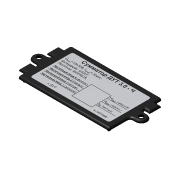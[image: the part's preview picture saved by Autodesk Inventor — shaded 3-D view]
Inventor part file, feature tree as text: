
AUTODESK INVENTOR PART (.ipt)
format: ipt  version: 2012 (Build 160160000, 160)  size: 340,480 bytes
history: native  units: mm
features: sketch x5, extrude x4, other x3, fillet x3
ambient origin geometry x8: Origin, YZ Plane, XZ Plane, XY Plane, X Axis, Y Axis, Z Axis, Center Point
feature tree (15):
  other  "Твердое тело1"
  extrude  "Выдавливание1"  Depth=65.0mm
  extrude  "Выдавливание2"  Depth=65.0mm
  extrude  "Выдавливание3"  Depth=4.0mm
  extrude  "Выдавливание4"  Depth=38.0mm
  fillet  "Сопряжение3"  Radius=8.0mm
  fillet  "Сопряжение4"  Radius=2.0mm
  fillet  "Сопряжение5"  Radius=2.0mm
  other  "Маркировка4"
  sketch  "Эскиз1"
  sketch  "Эскиз2"
  sketch  "Эскиз3"
  sketch  "Эскиз5"
  sketch  "Эскиз9"
  other  "Картинка7"
